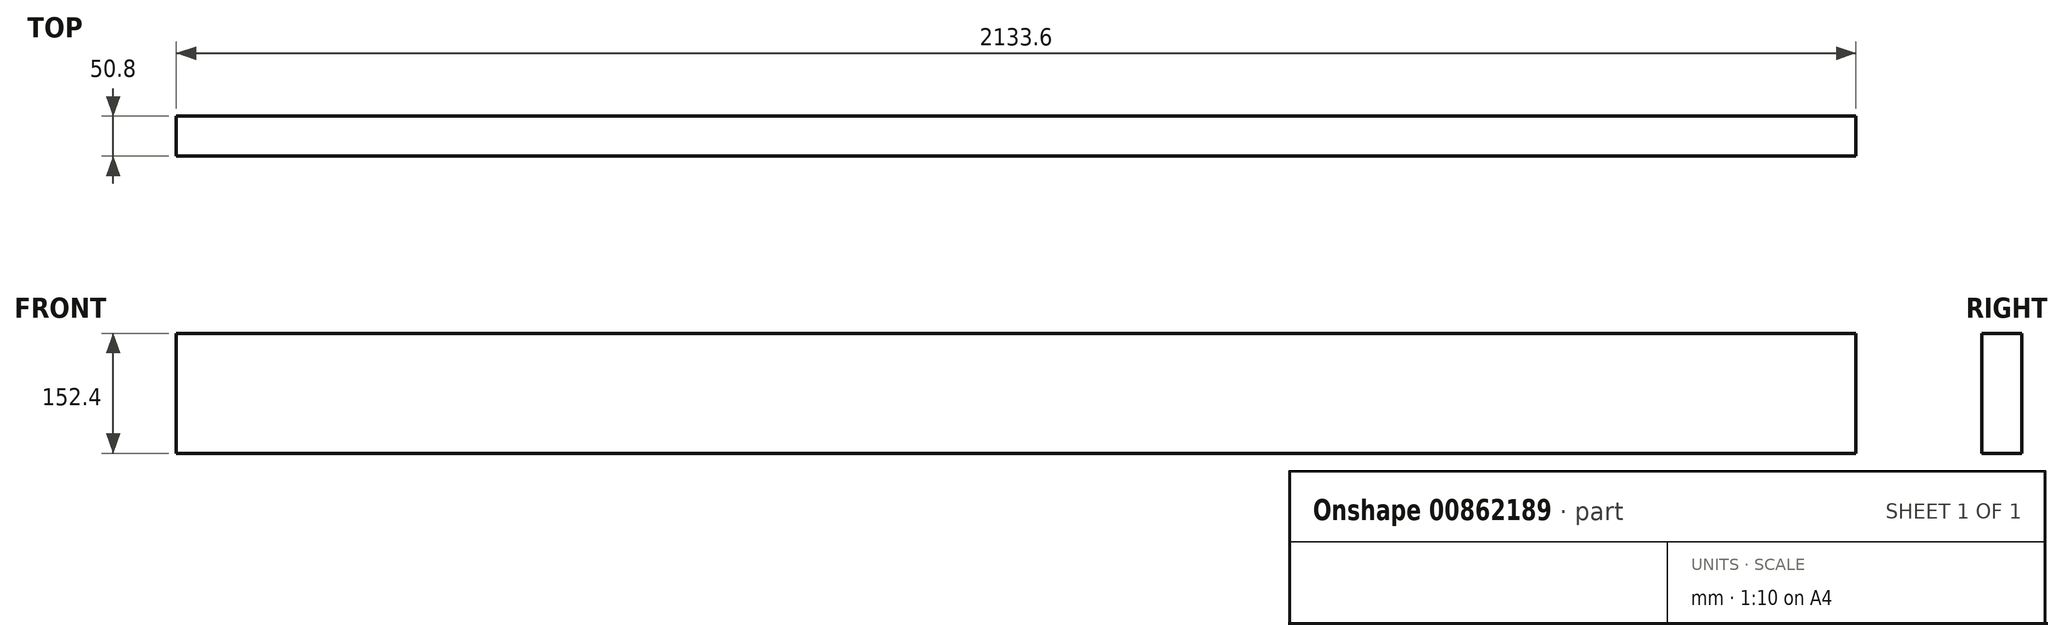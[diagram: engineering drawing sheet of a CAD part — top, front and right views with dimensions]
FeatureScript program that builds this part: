
annotation { "Feature Type Name" : "Feature", "Feature Type Description" : "" }
export const myFeature = defineFeature(function(context is Context, id is Id, definition is map)
    precondition{}
    {
        {
            var Q0;
            Q0=qCreatedBy(makeId("Front.planeOp"),FACE);
            var sketch = newSketch(context, id + "F0", { "sketchPlane" : qUnion([Q0])});
            skLineSegment(sketch, "E0.bottom", {"start": v(0, 0) * mm, "end": v(2133.6, 0) * mm});
            skLineSegment(sketch, "E0.top", {"start": v(0, 152.4) * mm, "end": v(2133.6, 152.4) * mm});
            skLineSegment(sketch, "E0.left", {"start": v(0, 0) * mm, "end": v(0, 152.4) * mm});
            skLineSegment(sketch, "E0.right", {"start": v(2133.6, 0) * mm, "end": v(2133.6, 152.4) * mm});
            skSolve(sketch);
        }
        {
            var Q0;
            Q0=makeQuery(id+"F0.imprint","IMPRINT",FACE,{"disambiguationData":[TD([[makeQuery(id+"F0.imprint","IMPRINT",EDGE,{"derivedFrom":sQuery(id+"F0.wireOp",EDGE,"E0.bottom")}),1.0]])]});
            extrude(context, id + "F1", {"entities" : qUnion([Q0]), "depth" : 50.8 * mm, "offsetDistance" : 25.4 * mm});
        }
    });
